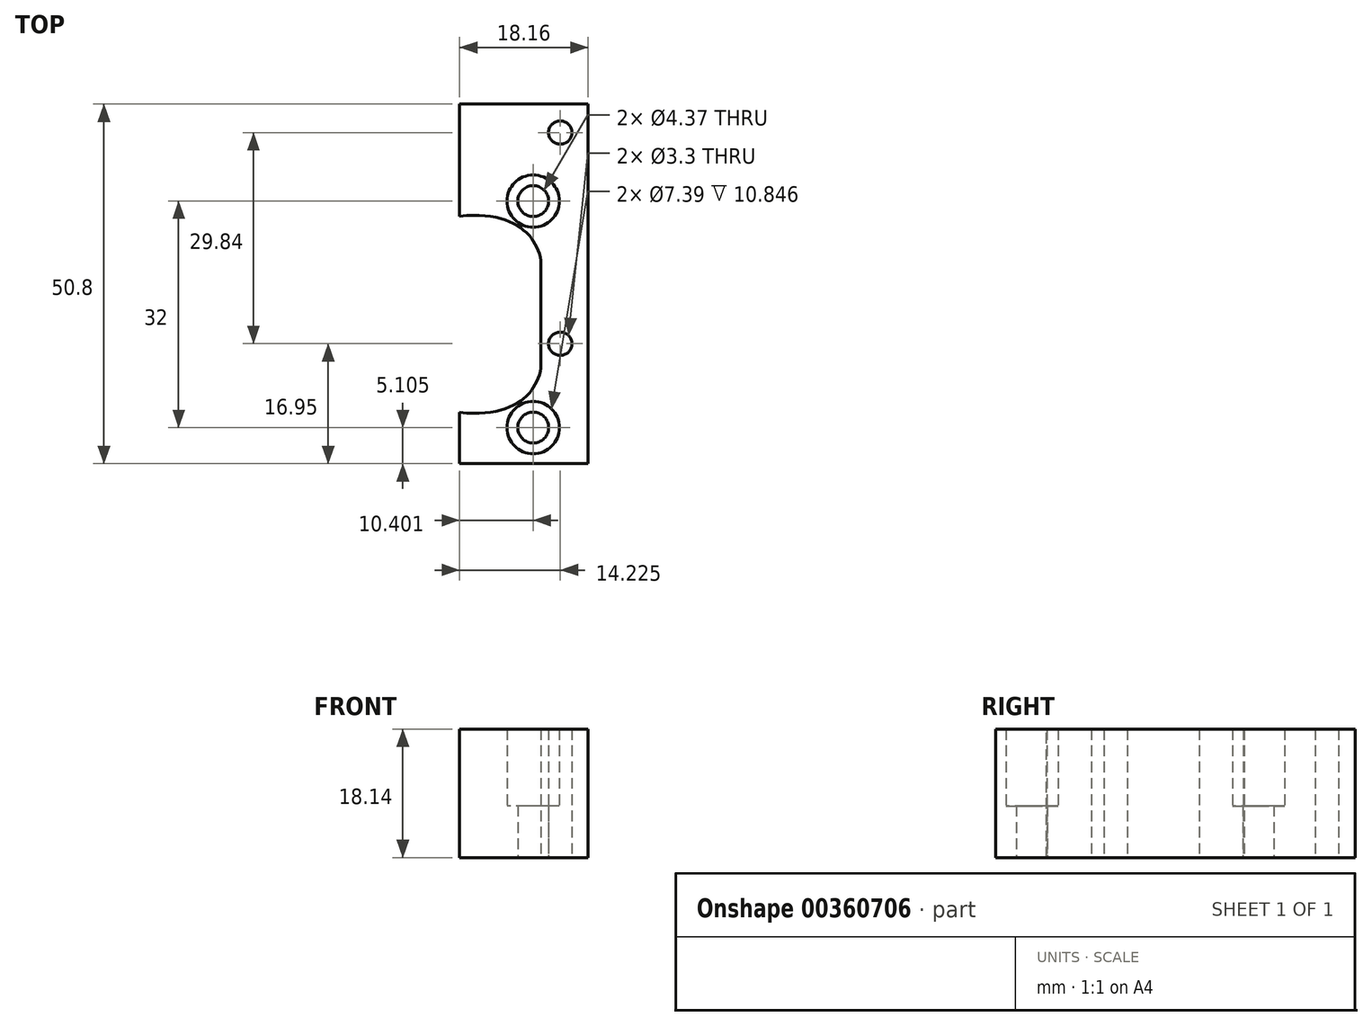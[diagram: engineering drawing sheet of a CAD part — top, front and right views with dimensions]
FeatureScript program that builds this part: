
annotation { "Feature Type Name" : "Feature", "Feature Type Description" : "" }
export const myFeature = defineFeature(function(context is Context, id is Id, definition is map)
    precondition{}
    {
        {
            var Q0;
            Q0=qCreatedBy(makeId("Top.planeOp"),FACE);
            var sketch = newSketch(context, id + "F0", { "sketchPlane" : qUnion([Q0])});
            skLineSegment(sketch, "E0.bottom", {"start": v(0, 0) * mm, "end": v(18.16, 0) * mm});
            skLineSegment(sketch, "E0.top", {"start": v(0, 50.8) * mm, "end": v(18.16, 50.8) * mm});
            skLineSegment(sketch, "E0.left", {"start": v(0, 0) * mm, "end": v(0, 7.24) * mm});
            skLineSegment(sketch, "E0.right", {"start": v(18.16, 0) * mm, "end": v(18.16, 50.8) * mm});
            skFitSpline(sketch, "E1", {"points": [v(0, 7.24) * mm, v(11.5, 13.49) * mm], "startDerivative": vector(23, -2.32) * mm, "endDerivative": vector(2.14, 10.95) * mm});
            skLineSegment(sketch, "E2", {"start": v(11.5, 13.49) * mm, "end": v(11.5, 21.1) * mm});
            skLineSegment(sketch, "E3", {"start": v(18.16, 21.1) * mm, "end": v(0, 21.1) * mm, "construction": true});
            skLineSegment(sketch, "E4.MirrorCS", {"start": v(11.5, 28.73) * mm, "end": v(11.5, 21.1) * mm});
            skFitSpline(sketch, "E5.MirrorCS", {"points": [v(0, 34.98) * mm, v(11.5, 28.73) * mm], "startDerivative": vector(23, 2.32) * mm, "endDerivative": vector(2.14, -10.95) * mm});
            skLineSegment(sketch, "E6.trimOffspring", {"start": v(0, 34.98) * mm, "end": v(0, 50.8) * mm});
            skLineSegment(sketch, "E7", {"start": v(14.22, 50.8) * mm, "end": v(14.22, 0) * mm, "construction": true});
            skCircle(sketch, "E8", {"center": v(14.22, 46.8) * mm, "radius": 1.65 * mm});
            skCircle(sketch, "E9", {"center": v(14.22, 16.95) * mm, "radius": 1.65 * mm});
            skCircle(sketch, "E10", {"center": v(10.4, 37.1) * mm, "radius": 3.7 * mm});
            skCircle(sketch, "E11", {"center": v(10.4, 5.1) * mm, "radius": 3.7 * mm});
            skLineSegment(sketch, "E12", {"start": v(10.4, 37.1) * mm, "end": v(10.4, 5.1) * mm, "construction": true});
            skCircle(sketch, "E13", {"center": v(10.4, 37.1) * mm, "radius": 2.18 * mm});
            skCircle(sketch, "E14", {"center": v(10.4, 5.1) * mm, "radius": 2.18 * mm});
            skSolve(sketch);
        }
        {
            var Q0;
            Q0=makeQuery(id+"F0.imprint","IMPRINT",FACE,{"disambiguationData":[TD([[makeQuery(id+"F0.imprint","IMPRINT",EDGE,{"derivedFrom":sQuery(id+"F0.wireOp",EDGE,"E0.bottom")}),1.0]])]});
            var Q1;
            Q1=makeQuery(id+"F0.imprint","IMPRINT",FACE,{"disambiguationData":[TD([[makeQuery(id+"F0.imprint","IMPRINT",EDGE,{"derivedFrom":sQuery(id+"F0.wireOp",EDGE,"E10")}),1.0]])]});
            var Q2;
            Q2=makeQuery(id+"F0.imprint","IMPRINT",FACE,{"disambiguationData":[TD([[makeQuery(id+"F0.imprint","IMPRINT",EDGE,{"derivedFrom":sQuery(id+"F0.wireOp",EDGE,"E11")}),1.0]])]});
            extrude(context, id + "F1", {"entities" : qUnion([Q0, Q1, Q2]), "depth" : 7.3 * mm});
        }
        {
            var Q0;
            Q0 = qSketchRegion(id + "F0", true);
            extrude(context, id + "F2", {"entities" : qUnion([Q0]), "operationType" : NewBodyOperationType.ADD, "depth" : 18.14 * mm});
        }
    });
